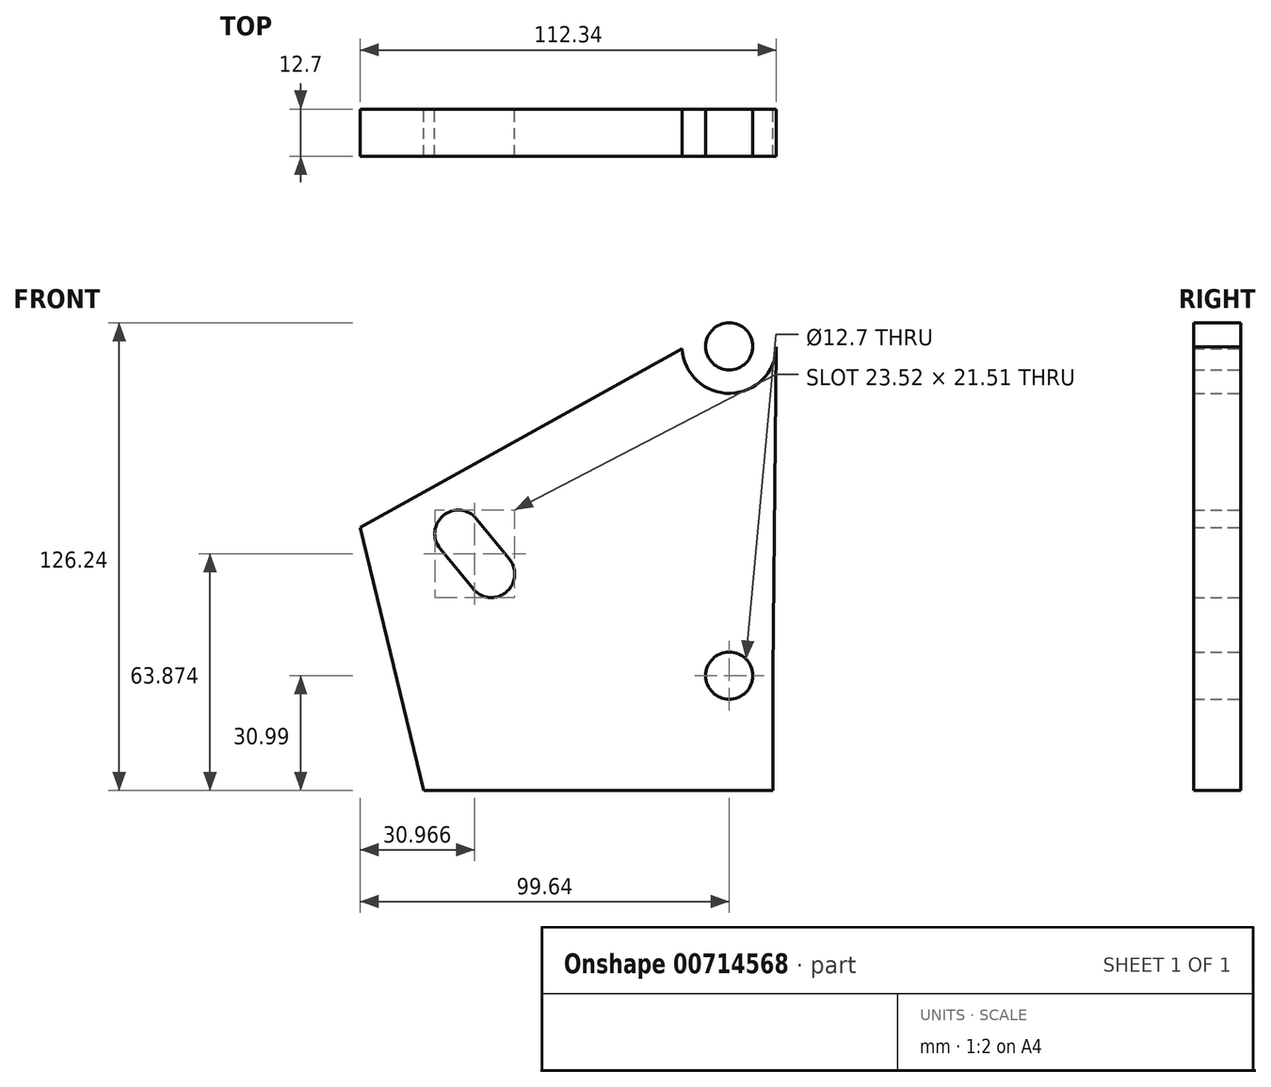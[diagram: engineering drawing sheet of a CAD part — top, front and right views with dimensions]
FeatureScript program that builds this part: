
annotation { "Feature Type Name" : "Feature", "Feature Type Description" : "" }
export const myFeature = defineFeature(function(context is Context, id is Id, definition is map)
    precondition{}
    {
        {
            var Q0;
            Q0=qCreatedBy(makeId("Front.planeOp"),FACE);
            var sketch = newSketch(context, id + "F0", { "sketchPlane" : qUnion([Q0])});
            skCircle(sketch, "E0", {"center": v(0, 88.9) * mm, "radius": 88.9 * mm, "construction": true});
            skCircle(sketch, "E1", {"center": v(0, 88.9) * mm, "radius": 6.35 * mm});
            skLineSegment(sketch, "E2", {"start": v(0, 0) * mm, "end": v(-73.11, 38.33) * mm, "construction": true});
            skLineSegment(sketch, "E3", {"start": v(-64.23, 27.44) * mm, "end": v(0, 0) * mm, "construction": true});
            skLineSegment(sketch, "E4", {"start": v(12.7, 88.77) * mm, "end": v(11.82, 0.79) * mm});
            skLineSegment(sketch, "E5", {"start": v(11.82, 0.79) * mm, "end": v(11.82, -31) * mm});
            skLineSegment(sketch, "E6.bottom", {"start": v(-99.64, 39.98) * mm, "end": v(-12.68, 88.2) * mm});
            skLineSegment(sketch, "E6.left", {"start": v(-99.64, 39.98) * mm, "end": v(-82.5, -31) * mm});
            skCircle(sketch, "E7", {"center": v(0, 88.9) * mm, "radius": 12.7 * mm});
            skCircle(sketch, "E8", {"center": v(0, 0) * mm, "radius": 6.35 * mm});
            skLineSegment(sketch, "E9", {"start": v(-82.5, -31) * mm, "end": v(11.82, -31) * mm});
            skLineSegment(sketch, "E10", {"start": v(-73.11, 38.33) * mm, "end": v(-64.23, 27.44) * mm});
            skArc(sketch, "E11.0.startCap", {"start": v(-78.03, 34.31) * mm, "mid": v(-77.13, 43.25) * mm, "end": v(-68.2, 42.34) * mm});
            skArc(sketch, "E11.0.endCap", {"start": v(-59.31, 31.45) * mm, "mid": v(-60.22, 22.52) * mm, "end": v(-69.15, 23.43) * mm});
            skLineSegment(sketch, "E11.0.left", {"start": v(-68.2, 42.34) * mm, "end": v(-59.31, 31.45) * mm});
            skLineSegment(sketch, "E11.0.right", {"start": v(-78.03, 34.31) * mm, "end": v(-69.15, 23.43) * mm});
            skSolve(sketch);
        }
        {
            var Q0;
            {var subQ0=sQuery(id+"F0.wireOp",EDGE,"E4");Q0=makeQuery(id+"F0.imprint","IMPRINT",FACE,{"disambiguationData":[TD([[makeQuery(id+"F0.imprint","IMPRINT",EDGE,{"derivedFrom":subQ0}),-1.0]])]});}
            var Q1;
            {var subQ12=sQuery(id+"F0.wireOp",EDGE,"E6.bottom");Q1=makeQuery(id+"F0.imprint","IMPRINT",FACE,{"disambiguationData":[TD([[makeQuery(id+"F0.imprint","IMPRINT",EDGE,{"derivedFrom":subQ12}),-1.0]])]});}
            var Q2;
            Q2=makeQuery(id+"F0.imprint","IMPRINT",FACE,{"disambiguationData":[TD([[makeQuery(id+"F0.imprint","IMPRINT",EDGE,{"derivedFrom":sQuery(id+"F0.wireOp",EDGE,"E1")}),1.0]])]});
            extrude(context, id + "F1", {"entities" : qUnion([Q0, Q1, Q2]), "depth" : 12.7 * mm, "offsetDistance" : 25.4 * mm});
        }
    });
